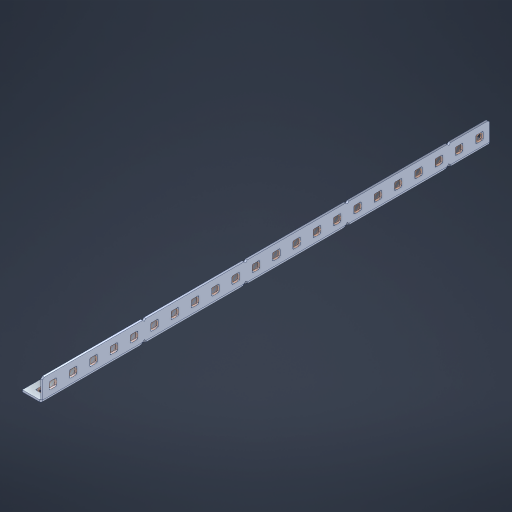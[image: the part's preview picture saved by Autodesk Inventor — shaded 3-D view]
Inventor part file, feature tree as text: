
AUTODESK INVENTOR PART (.ipt)
format: ipt  version: 2023 (Build 270158000, 158)  size: 788,480 bytes
history: native  units: in
note: dims shown in document units (in); Inventor stores cm internally (conversion verified against a paired STEP export)
features: other x49, extrude x43, sheet_metal_op x10, sketch x8, mirror x1, pattern_linear x1, chamfer x1
ambient origin geometry x8: Origin, YZ Plane, XZ Plane, XY Plane, X Axis, Y Axis, Z Axis, Center Point
bodies: Solid1 (feature_tree), Body (feature_tree)
feature tree (113):
  other  "Flange Pattern Plane"
  sheet_metal_op  "Flange Pattern"
  sheet_metal_op  "Body Pattern"
  other  "Arc Length"
  mirror  "Notch Mirror"
  pattern_linear  "Notch Pattern"  Spacing1=0.1875in  [1 undecoded]
  chamfer  "End Chamfer"
  extrude  "Half Cut"  Depth=0.0469in
  sketch  "Sketch1"  dims[d0=2.5in]
  other  "Plate1"
  sketch  "Sketch2"  dims[d1=11.0in]
  other  "Plate2"
  sheet_metal_op  "Bend1"
  sheet_metal_op  "Corner1"
  sketch  "Sketch3"  dims[d2=0.0469in]
  other  "Flange Pattern Sketch"
  sketch  "Sketch7"  dims[d3=0.0469in]
  other  "Srf1"
  other  "Srf2"
  sketch  "Sketch8"  dims[d4=0.0234in]
  sketch  "Sketch9"  dims[d5=0.0938in]
  other  "Srf91"
  sheet_metal_op  "Body Pattern Sketch"
  other  "Srf92"
  sketch  "Sketch13"  dims[d6=0.0469in]
  sketch  "Sketch14"  dims[d7=0.5in d8=90.0deg d9=0.0312in d10=0.1875in d11=0.0469in d12=0.0469in d16=0.182in d17=0.02in d18=0.0469in d19=0.0in d20=0.25in d21=0.25in d46=0.172in d47=1.0in d48=0.0in d49=0.182in d50=0.02in d51=0.25in d52=0.25in d53=0.0469in d54=0.0in d55=0.172in d56=1.0in d57=0.0in d60=8.6614in d62=0.5in d63=0.3937in d65=0.5in d85=0.1227in d86=0.1659in d88=0.04in d89=0.0469in d90=0.0in d91=0.04in d92=0.0491in d95=2.5in d96=0.04in d97=0.25in d98=45.0deg d101=0.0in d102=2.497in d131=0.5in d132=8.6614in d134=0.5in d139=0.5in]
  other  "Srf856"
  other  "Srf1310"
  other  "Srf1311"
  other  "Srf1312"
  other  "Srf1376"
  other  "Srf1377"
  other  "Srf1728"
  other  "Srf1755"
  other  "Srf1878"
  other  "Srf1879"
  other  "Srf1880"
  other  "Srf1881"
  other  "Srf1882"
  other  "Srf1883"
  other  "Srf1884"
  other  "Srf1885"
  other  "Srf1886"
  other  "Srf1887"
  other  "Srf1888"
  other  "Srf1889"
  other  "Srf1890"
  other  "Srf1891"
  other  "Srf1892"
  other  "Srf1893"
  other  "Srf1942"
  other  "Srf1943"
  other  "Srf1944"
  other  "Srf1945"
  other  "Srf1946"
  other  "Srf1947"
  other  "Srf1948"
  other  "Srf1949"
  other  "Srf1950"
  other  "Srf1951"
  other  "Srf1952"
  other  "Srf1953"
  other  "Srf1954"
  other  "Srf1955"
  other  "Srf1956"
  other  "Srf1957"
  sheet_metal_op  "Flange Stamp"
  sheet_metal_op  "Flange Circle"
  sheet_metal_op  "Body Stamp"
  sheet_metal_op  "Body Circle"
  sheet_metal_op  "Notch"
  extrude  "ExtrusionSrf2"  Depth=0.0469in
  extrude  "ExtrusionSrf92"  Depth=0.5in
  extrude  "ExtrusionSrf856"  Depth=0.02in
  extrude  "ExtrusionSrf1310"  Depth=0.0469in
  extrude  "ExtrusionSrf1311"  TaperAngle=0.0deg  [1 undecoded]
  extrude  "ExtrusionSrf1312"  Depth=0.5in
  extrude  "ExtrusionSrf1376"  Depth=0.5in
  extrude  "ExtrusionSrf1377"  Depth=0.5in
  extrude  "ExtrusionSrf1728"  Depth=0.5in TaperAngle=0.0deg
  extrude  "ExtrusionSrf1755"  Depth=0.5in
  extrude  "ExtrusionSrf1878"  Depth=0.02in
  extrude  "ExtrusionSrf1879"  Depth=0.5in
  extrude  "ExtrusionSrf1880"  Depth=0.5in
  extrude  "ExtrusionSrf1881"  Depth=0.0469in
  extrude  "ExtrusionSrf1882"  TaperAngle=0.0deg  [1 undecoded]
  extrude  "ExtrusionSrf1883"  Depth=0.5in
  extrude  "ExtrusionSrf1884"  Depth=0.5in TaperAngle=0.0deg
  extrude  "ExtrusionSrf1885"  Depth=0.5in
  extrude  "ExtrusionSrf1886"  Depth=0.5in
  extrude  "ExtrusionSrf1887"  Depth=0.5in
  extrude  "ExtrusionSrf1888"  Depth=0.5in
  extrude  "ExtrusionSrf1889"  Depth=0.5in
  extrude  "ExtrusionSrf1890"  Depth=0.0469in
  extrude  "ExtrusionSrf1891"  TaperAngle=0.0deg  [1 undecoded]
  extrude  "ExtrusionSrf1892"  Depth=0.5in
  extrude  "ExtrusionSrf1893"  Depth=0.5in
  extrude  "ExtrusionSrf1942"  Depth=0.5in
  extrude  "ExtrusionSrf1943"  Depth=0.5in TaperAngle=45.0deg
  extrude  "ExtrusionSrf1944"  TaperAngle=0.0deg  [1 undecoded]
  extrude  "ExtrusionSrf1945"  Depth=0.5in
  extrude  "ExtrusionSrf1946"  Depth=0.5in
  extrude  "ExtrusionSrf1947"  Depth=0.5in
  extrude  "ExtrusionSrf1948"  Depth=0.5in
  extrude  "ExtrusionSrf1949"  Depth=0.5in
  extrude  "ExtrusionSrf1950"  [1 undecoded]
  extrude  "ExtrusionSrf1951"  [1 undecoded]
  extrude  "ExtrusionSrf1952"  [1 undecoded]
  extrude  "ExtrusionSrf1953"  [1 undecoded]
  extrude  "ExtrusionSrf1954"  [1 undecoded]
  extrude  "ExtrusionSrf1955"  [1 undecoded]
  extrude  "ExtrusionSrf1956"  [1 undecoded]
  extrude  "ExtrusionSrf1957"  [1 undecoded]
note: 13 required parameter values undecoded (feature->parameter linkage not recoverable at this tier; creation-order binding heuristic only, values carry confidence <= 0.55)
